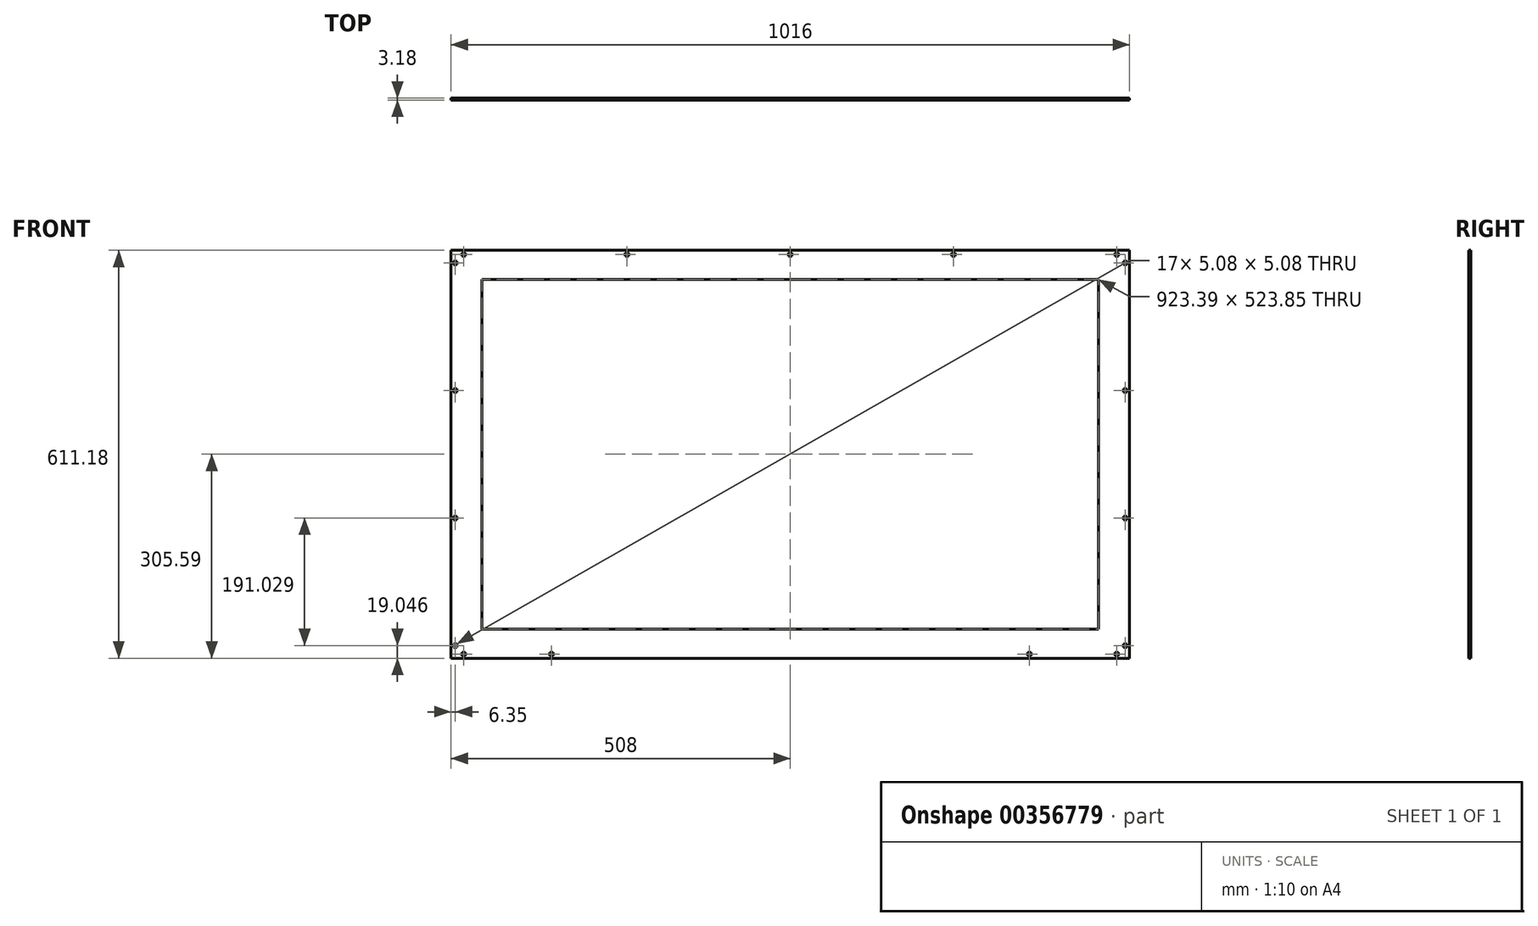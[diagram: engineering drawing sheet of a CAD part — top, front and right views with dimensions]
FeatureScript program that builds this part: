
annotation { "Feature Type Name" : "Feature", "Feature Type Description" : "" }
export const myFeature = defineFeature(function(context is Context, id is Id, definition is map)
    precondition{}
    {
        {
            var Q0;
            Q0=qCreatedBy(makeId("Front.planeOp"),FACE);
            var sketch = newSketch(context, id + "F0", { "sketchPlane" : qUnion([Q0])});
            skLineSegment(sketch, "E0.bottom", {"start": v(495.3, 292.9) * mm, "end": v(-495.3, 292.9) * mm});
            skLineSegment(sketch, "E0.top", {"start": v(495.3, -292.9) * mm, "end": v(-495.3, -292.9) * mm});
            skLineSegment(sketch, "E0.left", {"start": v(495.3, 292.9) * mm, "end": v(495.3, -292.9) * mm});
            skLineSegment(sketch, "E0.right", {"start": v(-495.3, 292.9) * mm, "end": v(-495.3, -292.9) * mm});
            skPoint(sketch, "E0.middle", {"position": v(0, 0) * mm});
            skLineSegment(sketch, "E1.0", {"start": v(-508, 305.6) * mm, "end": v(-508, -305.6) * mm});
            skLineSegment(sketch, "E1.1", {"start": v(508, 305.6) * mm, "end": v(-508, 305.6) * mm});
            skLineSegment(sketch, "E1.2", {"start": v(508, 305.6) * mm, "end": v(508, -305.6) * mm});
            skLineSegment(sketch, "E1.3", {"start": v(508, -305.6) * mm, "end": v(-508, -305.6) * mm});
            skLineSegment(sketch, "E2.bottom", {"start": v(-476, 276.23) * mm, "end": v(476, 276.23) * mm});
            skLineSegment(sketch, "E2.top", {"start": v(-476, -276.23) * mm, "end": v(476, -276.23) * mm});
            skLineSegment(sketch, "E2.left", {"start": v(-476, 276.23) * mm, "end": v(-476, -276.23) * mm});
            skLineSegment(sketch, "E2.right", {"start": v(476, 276.22) * mm, "end": v(476, -276.23) * mm});
            skLineSegment(sketch, "E3", {"start": v(-508, 305.6) * mm, "end": v(-495.3, 292.9) * mm});
            skPoint(sketch, "E4.middle", {"position": v(-501.65, 299.24) * mm});
            skLineSegment(sketch, "E5.bottom", {"start": v(-355.3, -296.7) * mm, "end": v(-360.38, -296.7) * mm});
            skLineSegment(sketch, "E5.top", {"start": v(-355.3, -301.78) * mm, "end": v(-360.38, -301.78) * mm});
            skLineSegment(sketch, "E5.left", {"start": v(-355.3, -296.7) * mm, "end": v(-355.3, -301.78) * mm});
            skLineSegment(sketch, "E5.right", {"start": v(-360.38, -296.7) * mm, "end": v(-360.38, -301.78) * mm});
            skPoint(sketch, "E5.middle", {"position": v(-357.84, -299.24) * mm});
            skLineSegment(sketch, "E6.MirrorCS", {"start": v(360.38, -296.7) * mm, "end": v(360.38, -301.78) * mm});
            skLineSegment(sketch, "E7.MirrorCS", {"start": v(355.3, -296.7) * mm, "end": v(360.38, -296.7) * mm});
            skLineSegment(sketch, "E8.MirrorCS", {"start": v(355.3, -296.7) * mm, "end": v(355.3, -301.78) * mm});
            skLineSegment(sketch, "E9.MirrorCS", {"start": v(355.3, -301.78) * mm, "end": v(360.38, -301.78) * mm});
            skLineSegment(sketch, "E10.bottom", {"start": v(461.7, 261.93) * mm, "end": v(-461.7, 261.93) * mm});
            skLineSegment(sketch, "E10.top", {"start": v(461.7, -261.93) * mm, "end": v(-461.7, -261.93) * mm});
            skLineSegment(sketch, "E10.left", {"start": v(461.7, 261.93) * mm, "end": v(461.7, -261.93) * mm});
            skLineSegment(sketch, "E10.right", {"start": v(-461.7, 261.93) * mm, "end": v(-461.7, -261.93) * mm});
            skLineSegment(sketch, "E11.bottom", {"start": v(-486.41, 296.7) * mm, "end": v(-491.5, 296.7) * mm});
            skLineSegment(sketch, "E11.top", {"start": v(-486.41, 301.78) * mm, "end": v(-491.5, 301.78) * mm});
            skLineSegment(sketch, "E11.left", {"start": v(-486.41, 296.7) * mm, "end": v(-486.41, 301.78) * mm});
            skLineSegment(sketch, "E11.right", {"start": v(-491.5, 296.7) * mm, "end": v(-491.5, 301.78) * mm});
            skPoint(sketch, "E11.middle", {"position": v(-488.95, 299.24) * mm});
            skLineSegment(sketch, "E12.MirrorCS", {"start": v(-504.19, 284) * mm, "end": v(-504.19, 289.08) * mm});
            skLineSegment(sketch, "E13.MirrorCS", {"start": v(-499.11, 289.08) * mm, "end": v(-504.2, 289.08) * mm});
            skLineSegment(sketch, "E14.MirrorCS", {"start": v(-499.11, 284) * mm, "end": v(-499.11, 289.08) * mm});
            skLineSegment(sketch, "E15.MirrorCS", {"start": v(-499.11, 284) * mm, "end": v(-504.2, 284) * mm});
            skCircle(sketch, "E16", {"center": v(-488.95, 299.24) * mm, "radius": 5.97 * mm});
            skLineSegment(sketch, "E17.MirrorCS", {"start": v(499.11, 284) * mm, "end": v(499.11, 289.08) * mm});
            skLineSegment(sketch, "E18.MirrorCS", {"start": v(499.11, 284) * mm, "end": v(504.2, 284) * mm});
            skLineSegment(sketch, "E19.MirrorCS", {"start": v(499.11, 289.08) * mm, "end": v(504.2, 289.08) * mm});
            skLineSegment(sketch, "E20.MirrorCS", {"start": v(504.19, 284) * mm, "end": v(504.19, 289.08) * mm});
            skLineSegment(sketch, "E21.MirrorCS", {"start": v(486.41, 301.78) * mm, "end": v(491.5, 301.78) * mm});
            skLineSegment(sketch, "E22.MirrorCS", {"start": v(486.41, 296.7) * mm, "end": v(486.41, 301.78) * mm});
            skLineSegment(sketch, "E23.MirrorCS", {"start": v(486.41, 296.7) * mm, "end": v(491.5, 296.7) * mm});
            skLineSegment(sketch, "E24.MirrorCS", {"start": v(491.5, 296.7) * mm, "end": v(491.5, 301.78) * mm});
            skPoint(sketch, "E25.MirrorP", {"position": v(488.95, 299.24) * mm});
            skLineSegment(sketch, "E26.MirrorCS", {"start": v(-499.11, -289.08) * mm, "end": v(-504.2, -289.08) * mm});
            skLineSegment(sketch, "E27.MirrorCS", {"start": v(-499.11, -284) * mm, "end": v(-499.11, -289.08) * mm});
            skLineSegment(sketch, "E28.MirrorCS", {"start": v(-499.11, -284) * mm, "end": v(-504.2, -284) * mm});
            skLineSegment(sketch, "E29.MirrorCS", {"start": v(-504.19, -284) * mm, "end": v(-504.19, -289.08) * mm});
            skLineSegment(sketch, "E30.MirrorCS", {"start": v(-486.41, -301.78) * mm, "end": v(-491.5, -301.78) * mm});
            skLineSegment(sketch, "E31.MirrorCS", {"start": v(-491.5, -296.7) * mm, "end": v(-491.5, -301.78) * mm});
            skPoint(sketch, "E32.MirrorP", {"position": v(-488.95, -299.24) * mm});
            skLineSegment(sketch, "E33.MirrorCS", {"start": v(-486.41, -296.7) * mm, "end": v(-486.41, -301.78) * mm});
            skLineSegment(sketch, "E34.MirrorCS", {"start": v(-486.41, -296.7) * mm, "end": v(-491.5, -296.7) * mm});
            skLineSegment(sketch, "E35.MirrorCS", {"start": v(486.41, -296.7) * mm, "end": v(486.41, -301.78) * mm});
            skPoint(sketch, "E36.MirrorP", {"position": v(488.95, -299.24) * mm});
            skLineSegment(sketch, "E37.MirrorCS", {"start": v(491.5, -296.7) * mm, "end": v(491.5, -301.78) * mm});
            skLineSegment(sketch, "E38.MirrorCS", {"start": v(486.41, -296.7) * mm, "end": v(491.5, -296.7) * mm});
            skLineSegment(sketch, "E39.MirrorCS", {"start": v(486.41, -301.78) * mm, "end": v(491.5, -301.78) * mm});
            skLineSegment(sketch, "E40.MirrorCS", {"start": v(499.11, -289.08) * mm, "end": v(504.2, -289.08) * mm});
            skLineSegment(sketch, "E41.MirrorCS", {"start": v(504.19, -284) * mm, "end": v(504.19, -289.08) * mm});
            skLineSegment(sketch, "E42.MirrorCS", {"start": v(499.11, -284) * mm, "end": v(499.11, -289.08) * mm});
            skLineSegment(sketch, "E43.MirrorCS", {"start": v(499.11, -284) * mm, "end": v(504.2, -284) * mm});
            skLineSegment(sketch, "E44.bottom", {"start": v(-504.19, 92.97) * mm, "end": v(-499.11, 92.97) * mm});
            skLineSegment(sketch, "E44.top", {"start": v(-504.19, 98.05) * mm, "end": v(-499.11, 98.05) * mm});
            skLineSegment(sketch, "E44.left", {"start": v(-504.2, 92.97) * mm, "end": v(-504.2, 98.05) * mm});
            skLineSegment(sketch, "E44.right", {"start": v(-499.11, 92.97) * mm, "end": v(-499.11, 98.05) * mm});
            skPoint(sketch, "E44.middle", {"position": v(-501.65, 95.51) * mm});
            skLineSegment(sketch, "E45.bottom", {"start": v(-499.11, -92.97) * mm, "end": v(-504.19, -92.97) * mm});
            skLineSegment(sketch, "E45.top", {"start": v(-499.11, -98.05) * mm, "end": v(-504.19, -98.05) * mm});
            skLineSegment(sketch, "E45.left", {"start": v(-499.11, -92.97) * mm, "end": v(-499.11, -98.05) * mm});
            skLineSegment(sketch, "E45.right", {"start": v(-504.2, -92.97) * mm, "end": v(-504.2, -98.05) * mm});
            skPoint(sketch, "E45.middle", {"position": v(-501.65, -95.51) * mm});
            skLineSegment(sketch, "E46", {"start": v(-501.65, -284) * mm, "end": v(-501.65, -98.05) * mm});
            skLineSegment(sketch, "E47", {"start": v(-501.65, -92.97) * mm, "end": v(-501.65, 92.97) * mm});
            skLineSegment(sketch, "E48", {"start": v(-501.65, 98.05) * mm, "end": v(-501.65, 284) * mm});
            skLineSegment(sketch, "E49.bottom", {"start": v(2.54, 301.78) * mm, "end": v(-2.54, 301.78) * mm});
            skLineSegment(sketch, "E49.top", {"start": v(2.54, 296.7) * mm, "end": v(-2.54, 296.7) * mm});
            skLineSegment(sketch, "E49.left", {"start": v(2.54, 301.78) * mm, "end": v(2.54, 296.7) * mm});
            skLineSegment(sketch, "E49.right", {"start": v(-2.54, 301.78) * mm, "end": v(-2.54, 296.7) * mm});
            skPoint(sketch, "E49.middle", {"position": v(0, 299.24) * mm});
            skPoint(sketch, "E49.middle.positionSnap0", {"position": v(0, 305.6) * mm});
            skPoint(sketch, "E49.centerSnap0", {"position": v(0, 305.6) * mm});
            skLineSegment(sketch, "E50.bottom", {"start": v(-241.94, 301.78) * mm, "end": v(-247.02, 301.78) * mm});
            skLineSegment(sketch, "E50.top", {"start": v(-241.94, 296.7) * mm, "end": v(-247.02, 296.7) * mm});
            skLineSegment(sketch, "E50.left", {"start": v(-241.94, 301.78) * mm, "end": v(-241.94, 296.7) * mm});
            skLineSegment(sketch, "E50.right", {"start": v(-247.02, 301.78) * mm, "end": v(-247.02, 296.7) * mm});
            skPoint(sketch, "E50.middle", {"position": v(-244.48, 299.24) * mm});
            skLineSegment(sketch, "E51.MirrorCS", {"start": v(241.94, 296.7) * mm, "end": v(247.02, 296.7) * mm});
            skPoint(sketch, "E52.MirrorP", {"position": v(244.48, 299.24) * mm});
            skLineSegment(sketch, "E53.MirrorCS", {"start": v(247.02, 301.78) * mm, "end": v(247.02, 296.7) * mm});
            skLineSegment(sketch, "E54.MirrorCS", {"start": v(241.94, 301.78) * mm, "end": v(247.02, 301.78) * mm});
            skLineSegment(sketch, "E55.MirrorCS", {"start": v(241.94, 301.78) * mm, "end": v(241.94, 296.7) * mm});
            skLineSegment(sketch, "E56.MirrorCS", {"start": v(504.19, 92.97) * mm, "end": v(499.11, 92.97) * mm});
            skLineSegment(sketch, "E57.MirrorCS", {"start": v(499.11, 92.97) * mm, "end": v(499.11, 98.05) * mm});
            skPoint(sketch, "E58.MirrorP", {"position": v(501.65, 95.51) * mm});
            skLineSegment(sketch, "E59.MirrorCS", {"start": v(504.19, 98.05) * mm, "end": v(499.11, 98.05) * mm});
            skLineSegment(sketch, "E60.MirrorCS", {"start": v(504.2, 92.97) * mm, "end": v(504.2, 98.05) * mm});
            skLineSegment(sketch, "E61.MirrorCS", {"start": v(499.11, -98.05) * mm, "end": v(504.19, -98.05) * mm});
            skLineSegment(sketch, "E62.MirrorCS", {"start": v(499.11, -92.97) * mm, "end": v(499.11, -98.05) * mm});
            skLineSegment(sketch, "E63.MirrorCS", {"start": v(499.11, -92.97) * mm, "end": v(504.19, -92.97) * mm});
            skPoint(sketch, "E64.MirrorP", {"position": v(501.65, -95.51) * mm});
            skLineSegment(sketch, "E65.MirrorCS", {"start": v(504.2, -92.97) * mm, "end": v(504.2, -98.05) * mm});
            skSolve(sketch);
        }
        {
            var Q0;
            {var subQ3=sQuery(id+"F0.wireOp",EDGE,"E0.left");Q0=makeQuery(id+"F0.imprint","IMPRINT",FACE,{"disambiguationData":[TD([[makeQuery(id+"F0.imprint","IMPRINT",EDGE,{"derivedFrom":subQ3}),-1.0]])]});}
            var Q1;
            {var subQ9=sQuery(id+"F0.wireOp",EDGE,"E0.left");Q1=makeQuery(id+"F0.imprint","IMPRINT",FACE,{"disambiguationData":[TD([[makeQuery(id+"F0.imprint","IMPRINT",EDGE,{"derivedFrom":subQ9}),1.0]])]});}
            var Q2;
            {var subQ1=sQuery(id+"F0.wireOp",EDGE,"O24vq0J8-WJNd-eW1m-mhOj-HjlkgafQAecY.top");Q2=makeQuery(id+"F0.imprint","IMPRINT",FACE,{"disambiguationData":[TD([[makeQuery(id+"F0.imprint","IMPRINT",EDGE,{"derivedFrom":subQ1}),1.0]])]});}
            var Q3;
            {var subQ9=sQuery(id+"F0.wireOp",EDGE,"O24vq0J8-WJNd-eW1m-mhOj-HjlkgafQAecY.bottom");Q3=makeQuery(id+"F0.imprint","IMPRINT",FACE,{"disambiguationData":[TD([[makeQuery(id+"F0.imprint","IMPRINT",EDGE,{"derivedFrom":subQ9}),-1.0]])]});}
            var Q4;
            {var subQ5=sQuery(id+"F0.wireOp",EDGE,"E0.right");Q4=makeQuery(id+"F0.imprint","IMPRINT",FACE,{"disambiguationData":[TD([[makeQuery(id+"F0.imprint","IMPRINT",EDGE,{"derivedFrom":subQ5}),-1.0]])]});}
            var Q5;
            {var subQ5=sQuery(id+"F0.wireOp",EDGE,"E4.bottom");Q5=makeQuery(id+"F0.imprint","IMPRINT",FACE,{"disambiguationData":[TD([[makeQuery(id+"F0.imprint","IMPRINT",EDGE,{"derivedFrom":subQ5}),-1.0]])]});}
            var Q6;
            {var subQ7=sQuery(id+"F0.wireOp",EDGE,"E4.right");Q6=makeQuery(id+"F0.imprint","IMPRINT",FACE,{"disambiguationData":[TD([[makeQuery(id+"F0.imprint","IMPRINT",EDGE,{"derivedFrom":subQ7}),-1.0]])]});}
            var Q7;
            {var subQ3=sQuery(id+"F0.wireOp",EDGE,"0pr6R6qP-uFYV-tloq-gIhA-llGfv03A3eT7");var subQ5=sQuery(id+"F0.wireOp",EDGE,"hnryXjpA-dOW9-xkJg-QQz7-FwJbjo40cldU");var subQ6=makeQuery(id+"F0.imprint","INTERSECT",VERTEX,{"derivedFrom":[subQ3,subQ5]});Q7=makeQuery(id+"F0.imprint","IMPRINT",FACE,{"disambiguationData":[TD([[makeQuery(id+"F0.imprint","IMPRINT",EDGE,{"disambiguationData":[TD([[subQ6,-1.0]])],"derivedFrom":subQ3}),1.0]])]});}
            var Q8;
            {var subQ1=sQuery(id+"F0.wireOp",EDGE,"E3");var subQ3=sQuery(id+"F0.wireOp",EDGE,"0pr6R6qP-uFYV-tloq-gIhA-llGfv03A3eT7");var subQ4=makeQuery(id+"F0.imprint","INTERSECT",VERTEX,{"disambiguationData":[OD(1.0)],"derivedFrom":[subQ1,subQ3]});Q8=makeQuery(id+"F0.imprint","IMPRINT",FACE,{"disambiguationData":[TD([[makeQuery(id+"F0.imprint","IMPRINT",EDGE,{"disambiguationData":[TD([[subQ4,-1.0]])],"derivedFrom":subQ3}),1.0]])]});}
            var Q9;
            Q9=makeQuery(id+"F0.imprint","IMPRINT",FACE,{"disambiguationData":[TD([[makeQuery(id+"F0.imprint","IMPRINT",EDGE,{"derivedFrom":sQuery(id+"F0.wireOp",EDGE,"E2.bottom")}),-1.0]])]});
            var Q10;
            Q10=makeQuery(id+"F0.imprint","IMPRINT",FACE,{"disambiguationData":[TD([[makeQuery(id+"F0.imprint","IMPRINT",EDGE,{"derivedFrom":sQuery(id+"F0.wireOp",EDGE,"E11.bottom")}),1.0]])]});
            extrude(context, id + "F1", {"entities" : qUnion([Q0, Q1, Q2, Q3, Q4, Q5, Q6, Q7, Q8, Q9, Q10]), "endBound" : BoundingType.SYMMETRIC, "oppositeDirection" : true, "depth" : 3.17 * mm});
        }
    });
